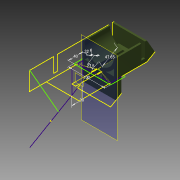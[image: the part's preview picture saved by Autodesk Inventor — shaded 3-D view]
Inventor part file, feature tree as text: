
AUTODESK INVENTOR PART (.ipt)
format: ipt  version: 2013 (Build 170138000, 138)  size: 288,768 bytes
history: native  units: mm
features: sketch x16, extrude x10, other x3, hole x1
ambient origin geometry x8: Origin, YZ Plane, XZ Plane, XY Plane, X Axis, Y Axis, Z Axis, Center Point
feature tree (30):
  other  "ソリッド1"
  extrude  "押し出し1"  Depth=90.0mm
  extrude  "押し出し2"  Depth=50.0mm
  extrude  "押し出し3"  Depth=5.0mm
  extrude  "押し出し4"  Depth=85.0mm
  extrude  "押し出し6"  Depth=5.0mm
  sketch  "スケッチ9"
  hole  "穴1"  [1 undecoded]
  extrude  "押し出し12"  Depth=10.0mm
  sketch  "スケッチ19"
  sketch  "スケッチ20"
  other  "作業平面5"
  extrude  "押し出し13"  Depth=90.0mm
  other  "作業平面6"
  extrude  "押し出し14"  Depth=230.0mm TaperAngle=0.0deg
  extrude  "押し出し15"  Depth=225.0mm TaperAngle=0.0deg
  sketch  "スケッチ24"
  sketch  "スケッチ25"
  extrude  "押し出し16"  Depth=5.0mm TaperAngle=0.0deg
  sketch  "スケッチ1"
  sketch  "スケッチ2"
  sketch  "スケッチ3"
  sketch  "スケッチ4"
  sketch  "スケッチ6"
  sketch  "スケッチ11"
  sketch  "スケッチ18"
  sketch  "スケッチ21"
  sketch  "スケッチ22"
  sketch  "スケッチ23"
  sketch  "スケッチ26"
note: 1 required parameter value undecoded (feature->parameter linkage not recoverable at this tier; creation-order binding heuristic only, values carry confidence <= 0.55)
